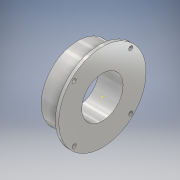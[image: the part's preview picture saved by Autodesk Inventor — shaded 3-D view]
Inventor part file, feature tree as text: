
AUTODESK INVENTOR PART (.ipt)
format: ipt  version: 2017.3 (Build 213256000, 256)  size: 147,456 bytes
history: native  units: mm
features: sketch x6, extrude x4, hole x1
ambient origin geometry x8: Origin, YZ Plane, XZ Plane, XY Plane, X Axis, Y Axis, Z Axis, Center Point
bodies: Solid1 (feature_tree)
feature tree (11):
  extrude  "Extrusion1"  Depth=1.0mm TaperAngle=0.0deg
  extrude  "Extrusion2"  Depth=6.5mm TaperAngle=0.0deg
  hole  "Hole1"  [1 undecoded]
  sketch  "Sketch4"  dims[d14=1.67mm d15=1.67mm]
  extrude  "Extrusion3"  Depth=1.67mm
  extrude  "Extrusion4"  Depth=1.67mm
  sketch  "Sketch1"  dims[d0=26.4mm d1=1.0mm d2=0.0mm]
  sketch  "Sketch2"  dims[d3=22.0mm d4=6.5mm d5=0.0mm]
  sketch  "Sketch3"  dims[d6=1.221mm d7=3.2mm d8=4.0mm d9=2.0mm d10=90.0deg d11=5.3mm d12=20.594885mm d13=1.67mm]
  sketch  "Sketch5"  dims[d16=1.67mm d17=1.67mm]
  sketch  "Sketch6"  dims[d18=1.67mm d19=1.0mm d20=0.0mm d21=12.5mm d22=10.0mm d23=0.0mm]
note: 1 required parameter value undecoded (feature->parameter linkage not recoverable at this tier; creation-order binding heuristic only, values carry confidence <= 0.55)
